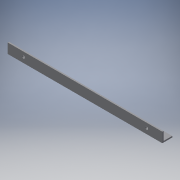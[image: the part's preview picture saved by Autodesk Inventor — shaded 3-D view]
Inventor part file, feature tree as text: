
AUTODESK INVENTOR PART (.ipt)
format: ipt  version: 2018 (Build 220112000, 112)  size: 128,000 bytes
history: native  units: mm
features: extrude x4, sketch x4
ambient origin geometry x8: Origin, YZ Plane, XZ Plane, XY Plane, X Axis, Y Axis, Z Axis, Center Point
bodies: Solid1 (feature_tree)
feature tree (8):
  extrude  "Extrusion1"  Depth=15.08mm
  extrude  "Extrusion2"  Depth=2.05mm
  extrude  "Extrusion3"  Depth=13.03mm
  extrude  "Extrusion4"  Depth=2.05mm
  sketch  "Sketch1"  dims[d0=234.5mm d1=15.08mm]
  sketch  "Sketch2"  dims[d2=2.05mm d3=0.0mm d4=2.05mm]
  sketch  "Sketch3"  dims[d5=13.03mm d6=0.0mm d7=93.5mm]
  sketch  "Sketch4"  dims[d8=93.5mm d9=8.0mm d10=8.0mm d11=2.05mm d12=0.0mm d13=4.2mm d14=4.2mm d15=4.2mm d16=4.2mm d17=8.0mm d18=93.5mm d19=93.5mm d20=8.0mm d21=2.05mm d22=0.0mm]
